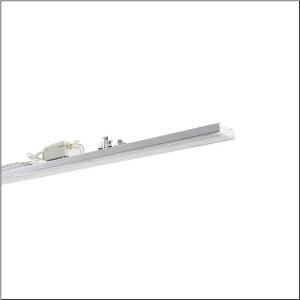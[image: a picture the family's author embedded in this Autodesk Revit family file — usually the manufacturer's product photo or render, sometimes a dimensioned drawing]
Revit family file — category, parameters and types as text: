
# Revit family: licross_11_recessed_mo_51tl11dn4axg
name_source: partatom
category: Lighting Fixtures
units: mm (PartAtom-declared; Revit-internal decimal feet)

## family parameters
Cut with Voids When Loaded = No
Host = Face
Light Source = No
Part Type = Normal
Room Calculation Point = No
Round Connector Dimension = Use Diameter
Shared = No

## types (1)
- --- (1 x LED, 10080 lm, 56.7 W, 4000K)
    Apparent Load = 57 VA
    CIE Flux Codes = 89 96 99 100 100
    Color Rendering = 80
    Color Temperature = 4000K
    Default Elevation = 1800 mm
    Description = Licross 11 Recessed MO, luminaire insert, of sheet steel, coil coated, white, length: 1.500mm, width: 66mm, height: 67mm, LED rated luminous flux: 10.080lm, light colour: 840, SDCM (Standard Deviation of Colour Matching)MacAdam ≤ 2 SDCM (initial), control gear: DALI 2, with plug, 5-pole, with phase selection, mains connection: 220..240V, AC, 50/60Hz, rated input power: 57W, internal wiring halogen-free, primary light control with lens, of plastic, primary optical cover: cover, of PMMA, light emission: direct distribution, primary light characteristic: symmetric, protection rating (complete): IP40, insulation class (complete): insulation class I (protective earthing), certification: CE, ENEC, VDE, UKCA, protection symbol: D if used in an environment without relevant dust loads with corresponding accessories, impact resistance: IK06, permissible ambient temperature for indoor applications: -25..+35°C, corresponds to IFS (International Featured Standards) requirements for safety and quality in the food industry, reducing of maximum allowable ambient temperature of 5°C with ceiling mounting, LABS conformity tested according to VDMA 24364:2018-05, The light source and the operating device comply with the requirements of the Ecodesign Regulation (EU) 2019/2020 and are replaceable in accordance with this regulation, packaging unit: 1 piece
    Height = 58 mm
    Lamp = 1 x LED
    Lamp Light Flux = 10080 lm
    Lamp Power = 56.7 W
    Lamp count = 1
    Length = 1500 mm
    Luminous efficacy = 178 lm/W
    Manufacturer = Siteco
    ModVariant = No
    Model = 51TL11DN4AXG
    Mounting Place = Ceiling
    Mounting Type = Pendant
    Number of Poles = 1
    OnlyDefault = Yes
    Power Factor = 1
    Product Name = Licross 11 Recessed MO
    Product group = luminaire insert | ceiling pendant
    ProductGroupID = 901
    Protection Class = Protection class I
    Protection Degree = IP 40
    RLX_Detail_Level = 1
    RLX_Emergency_Light_Flux = 0 lm
    RLX_Emergency_Type = 0
    RLX_Emergency_Type_DB = No
    RlxData = <blob elided: 24757 chars, md5=90def551>
    Socket = socket
    Standby Power = 0 W
    System Light Flux = 10080 lm
    System Power = 57 W
    Type Comments = factory setting: luminous flux: 100 % | dim-lin: 254 | 378 mA
    Type Image = l_1296930.jpg
    URL = http://relux.com
    VarID = @adj_101835
    Voltage = 0 V
    Weight = 0.00 kg
    Width = 66 mm

## geometry (parser evidence)
native form markers: Blend x4, Sweep x10
no freeform markers — native parametric forms only
